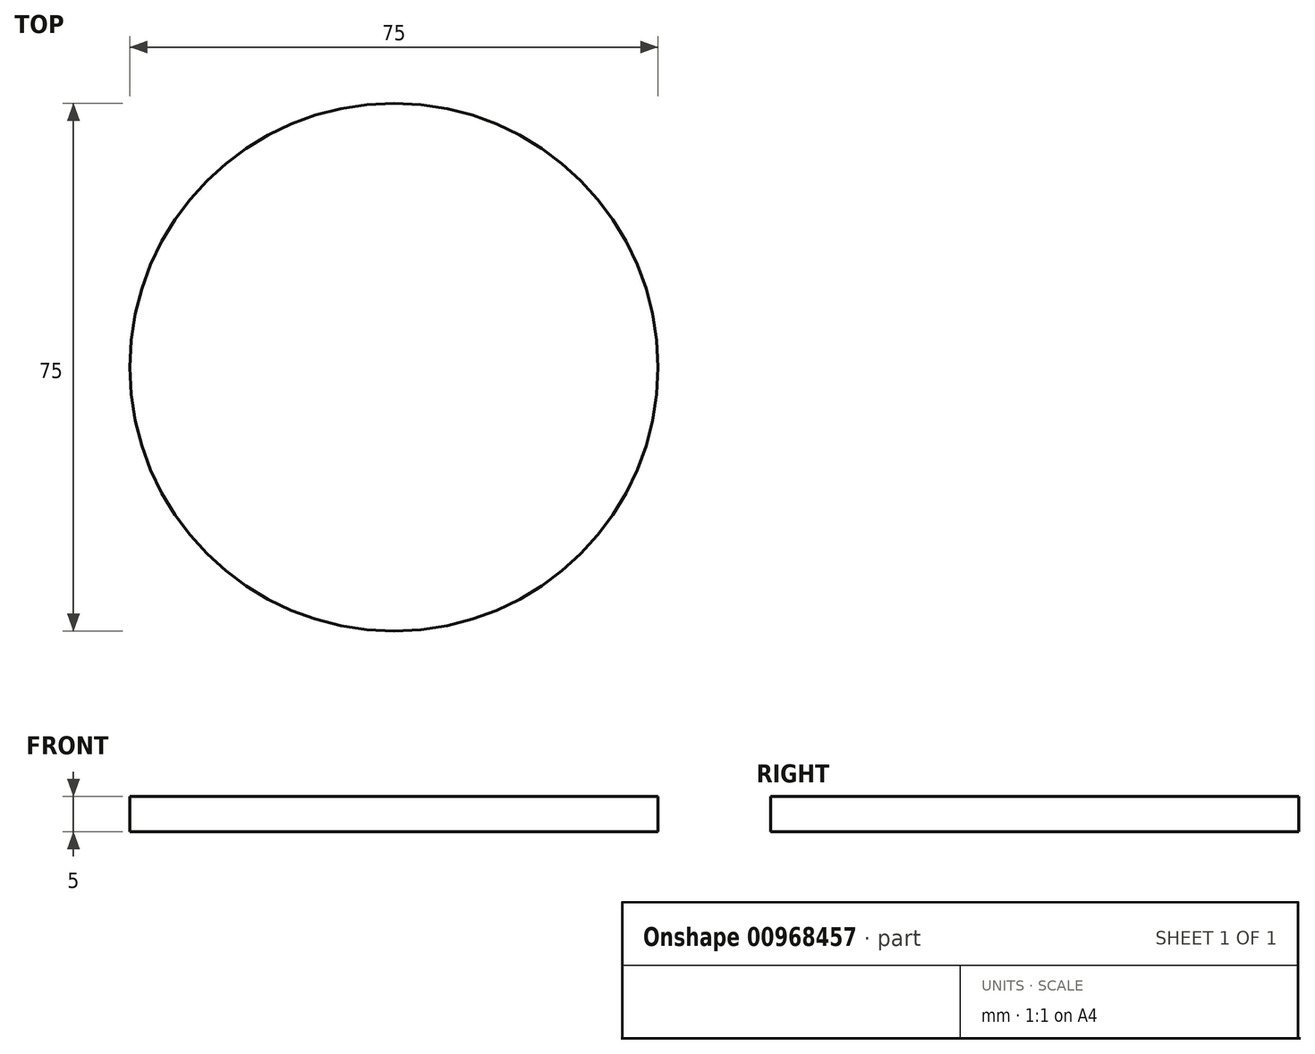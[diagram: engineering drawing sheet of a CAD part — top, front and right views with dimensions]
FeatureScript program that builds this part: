
annotation { "Feature Type Name" : "Feature", "Feature Type Description" : "" }
export const myFeature = defineFeature(function(context is Context, id is Id, definition is map)
    precondition{}
    {
        {
            var Q0;
            Q0=qCreatedBy(makeId("Top.planeOp"),FACE);
            var sketch = newSketch(context, id + "F0", { "sketchPlane" : qUnion([Q0])});
            skLineSegment(sketch, "E0.bottom", {"start": v(0, 0) * mm, "end": v(18, 0) * mm});
            skLineSegment(sketch, "E0.top", {"start": v(0, 65) * mm, "end": v(18, 65) * mm});
            skLineSegment(sketch, "E0.left", {"start": v(0, 0) * mm, "end": v(0, 65) * mm});
            skLineSegment(sketch, "E0.right", {"start": v(18, 0) * mm, "end": v(18, 65) * mm});
            skLineSegment(sketch, "E1", {"start": v(0, 0) * mm, "end": v(18, 65) * mm});
            skLineSegment(sketch, "E2", {"start": v(0, 65) * mm, "end": v(18, 0) * mm});
            skCircle(sketch, "E3", {"center": v(9, 32.5) * mm, "radius": 37.5 * mm});
            skSolve(sketch);
        }
        {
            var Q0;
            Q0=makeQuery(id+"F0.imprint","IMPRINT",FACE,{"disambiguationData":[TD([[makeQuery(id+"F0.imprint","IMPRINT",EDGE,{"derivedFrom":sQuery(id+"F0.wireOp",EDGE,"E0.bottom")}),-1.0]])]});
            var Q1;
            {var subQ0=sQuery(id+"F0.wireOp",EDGE,"E0.top");Q1=makeQuery(id+"F0.imprint","IMPRINT",FACE,{"disambiguationData":[TD([[makeQuery(id+"F0.imprint","IMPRINT",EDGE,{"derivedFrom":subQ0}),-1.0]])]});}
            var Q2;
            {var subQ0=sQuery(id+"F0.wireOp",EDGE,"E0.right");Q2=makeQuery(id+"F0.imprint","IMPRINT",FACE,{"disambiguationData":[TD([[makeQuery(id+"F0.imprint","IMPRINT",EDGE,{"derivedFrom":subQ0}),1.0]])]});}
            var Q3;
            {var subQ0=sQuery(id+"F0.wireOp",EDGE,"E0.bottom");Q3=makeQuery(id+"F0.imprint","IMPRINT",FACE,{"disambiguationData":[TD([[makeQuery(id+"F0.imprint","IMPRINT",EDGE,{"derivedFrom":subQ0}),1.0]])]});}
            var Q4;
            {var subQ0=sQuery(id+"F0.wireOp",EDGE,"E0.left");Q4=makeQuery(id+"F0.imprint","IMPRINT",FACE,{"disambiguationData":[TD([[makeQuery(id+"F0.imprint","IMPRINT",EDGE,{"derivedFrom":subQ0}),-1.0]])]});}
            extrude(context, id + "F1", {"entities" : qUnion([Q0, Q1, Q2, Q3, Q4]), "depth" : 5 * mm, "offsetDistance" : 25 * mm});
        }
    });
